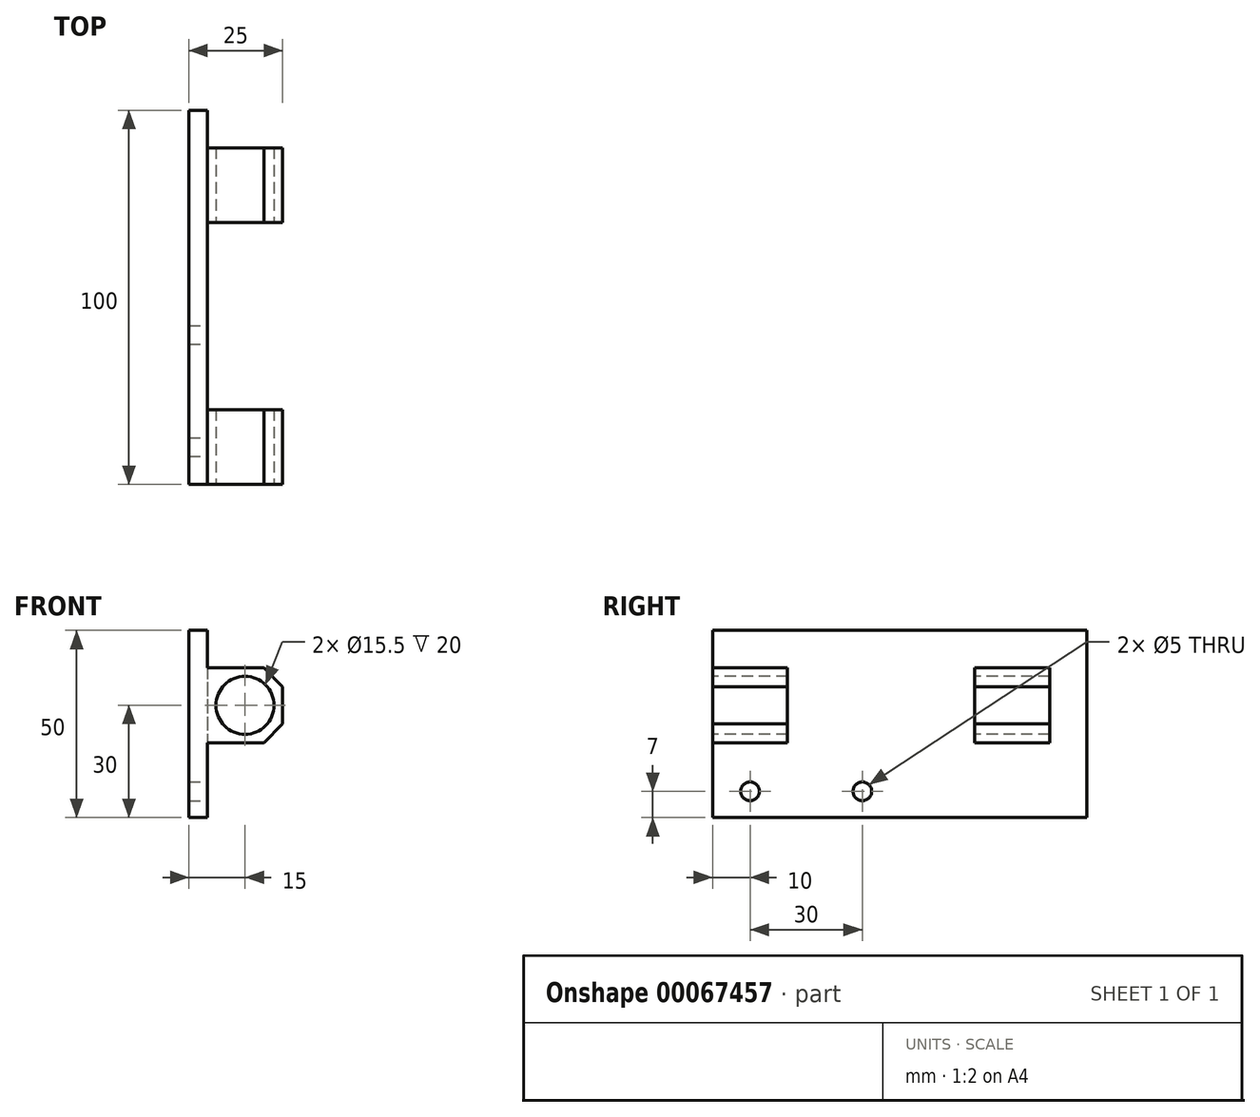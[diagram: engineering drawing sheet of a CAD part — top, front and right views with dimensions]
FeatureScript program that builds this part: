
annotation { "Feature Type Name" : "Feature", "Feature Type Description" : "" }
export const myFeature = defineFeature(function(context is Context, id is Id, definition is map)
    precondition{}
    {
        {
            var Q0;
            Q0=qCreatedBy(makeId("Front.planeOp"),FACE);
            var sketch = newSketch(context, id + "F0", { "sketchPlane" : qUnion([Q0])});
            skLineSegment(sketch, "E0.bottom", {"start": v(0, 0) * mm, "end": v(-5, 0) * mm});
            skLineSegment(sketch, "E0.top", {"start": v(0, -50) * mm, "end": v(-5, -50) * mm});
            skLineSegment(sketch, "E0.left", {"start": v(0, 0) * mm, "end": v(0, -50) * mm});
            skLineSegment(sketch, "E0.right", {"start": v(-5, 0) * mm, "end": v(-5, -50) * mm});
            skSolve(sketch);
        }
        {
            var Q0;
            Q0 = qSketchRegion(id + "F0", true);
            extrude(context, id + "F1", {"entities" : qUnion([Q0]), "oppositeDirection" : true, "depth" : 100 * mm});
        }
        {
            var Q0;
            Q0=makeQuery(id+"F1.opExtrude","SWEPT_FACE",FACE,{"disambiguationData":[OSD([sQuery(id+"F0.wireOp",EDGE,"E0.left")])]});
            var sketch = newSketch(context, id + "F2", { "sketchPlane" : qUnion([Q0])});
            skPoint(sketch, "E1", {"position": v(10, -43) * mm});
            skPoint(sketch, "E2", {"position": v(40, -43) * mm});
            skLineSegment(sketch, "E3.bottom", {"start": v(0, -10) * mm, "end": v(20, -10) * mm});
            skLineSegment(sketch, "E3.top", {"start": v(0, -30) * mm, "end": v(20, -30) * mm});
            skLineSegment(sketch, "E3.left", {"start": v(0, -10) * mm, "end": v(0, -30) * mm});
            skLineSegment(sketch, "E3.right", {"start": v(20, -10) * mm, "end": v(20, -30) * mm});
            skLineSegment(sketch, "E4.bottom", {"start": v(70, -10) * mm, "end": v(90, -10) * mm});
            skLineSegment(sketch, "E4.top", {"start": v(70, -30) * mm, "end": v(90, -30) * mm});
            skLineSegment(sketch, "E4.left", {"start": v(70, -10) * mm, "end": v(70, -30) * mm});
            skLineSegment(sketch, "E4.right", {"start": v(90, -10) * mm, "end": v(90, -30) * mm});
            skSolve(sketch);
        }
        {
            var Q0;
            Q0=sQuery(id+"F2.wireOp",VERTEX,"E1");
            var Q1;
            Q1=sQuery(id+"F2.wireOp",VERTEX,"E2");
            var Q2;
            Q2=makeQuery(id+"F1.opExtrude","SWEPT_BODY",BODY,{"disambiguationData":[OSD([sQuery(id+"F0.wireOp",EDGE,"E0.bottom"),sQuery(id+"F0.wireOp",EDGE,"E0.top"),sQuery(id+"F0.wireOp",EDGE,"E0.left"),sQuery(id+"F0.wireOp",EDGE,"E0.right")])]});
            hole(context, id + "F3", {"style" : HoleStyle.SIMPLE, "holeDiameter" : 5 * mm, "endStyle" : HoleEndStyle.THROUGH, "locations" : qUnion([Q0, Q1]), "scope" : qUnion([Q2])});
        }
        {
            var Q0;
            Q0 = qSketchRegion(id + "F2", true);
            extrude(context, id + "F4", {"entities" : qUnion([Q0]), "operationType" : NewBodyOperationType.ADD, "depth" : 20 * mm});
        }
        {
            var Q0;
            Q0=makeQuery(id+"F4.opExtrude","CAP_EDGE",EDGE,{"disambiguationData":[OSD([sQuery(id+"F2.wireOp",EDGE,"E3.bottom")])],"isStart":false});
            var Q1;
            Q1=makeQuery(id+"F4.opExtrude","CAP_EDGE",EDGE,{"disambiguationData":[OSD([sQuery(id+"F2.wireOp",EDGE,"E3.top")])],"isStart":false});
            var Q2;
            Q2=makeQuery(id+"F4.opExtrude","CAP_EDGE",EDGE,{"disambiguationData":[OSD([sQuery(id+"F2.wireOp",EDGE,"E4.bottom")])],"isStart":false});
            var Q3;
            Q3=makeQuery(id+"F4.opExtrude","CAP_EDGE",EDGE,{"disambiguationData":[OSD([sQuery(id+"F2.wireOp",EDGE,"E4.top")])],"isStart":false});
            chamfer(context, id + "F5", {"entities" : qUnion([Q0, Q1, Q2, Q3]), "width" : 5 * mm, "tangentPropagation" : true});
        }
        {
            var Q0;
            Q0=makeQuery(id+"F4.boolean.opBoolean","MERGE",FACE,{"derivedFrom":[makeQuery(id+"F1.opExtrude","CAP_FACE",FACE,{"disambiguationData":[OSD([sQuery(id+"F0.wireOp",EDGE,"E0.bottom"),sQuery(id+"F0.wireOp",EDGE,"E0.top"),sQuery(id+"F0.wireOp",EDGE,"E0.left"),sQuery(id+"F0.wireOp",EDGE,"E0.right")])],"isStart":true}),makeQuery(id+"F4.opExtrude","SWEPT_FACE",FACE,{"disambiguationData":[OSD([sQuery(id+"F2.wireOp",EDGE,"E3.left")])]})]});
            var sketch = newSketch(context, id + "F6", { "sketchPlane" : qUnion([Q0])});
            skPoint(sketch, "E5", {"position": v(10, -20) * mm});
            skSolve(sketch);
        }
        {
            var Q0;
            Q0=sQuery(id+"F6.wireOp",VERTEX,"E5");
            var Q1;
            Q1=makeQuery(id+"F1.opExtrude","SWEPT_BODY",BODY,{"disambiguationData":[OSD([sQuery(id+"F0.wireOp",EDGE,"E0.bottom"),sQuery(id+"F0.wireOp",EDGE,"E0.top"),sQuery(id+"F0.wireOp",EDGE,"E0.left"),sQuery(id+"F0.wireOp",EDGE,"E0.right")])]});
            hole(context, id + "F7", {"style" : HoleStyle.SIMPLE, "holeDiameter" : 15.5 * mm, "endStyle" : HoleEndStyle.THROUGH, "locations" : qUnion([Q0]), "scope" : qUnion([Q1])});
        }
    });
